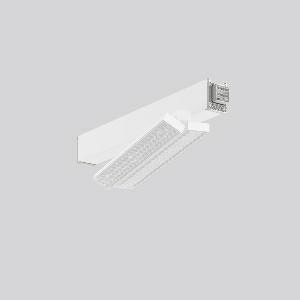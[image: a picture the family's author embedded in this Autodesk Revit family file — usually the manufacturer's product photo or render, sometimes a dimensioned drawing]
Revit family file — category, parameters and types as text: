
# Revit family: linedo_strahlermodule_-_tx-move_950690_842_776_400_4c77
name_source: partatom
category: Lighting Fixtures
units: mm (PartAtom-declared; Revit-internal decimal feet)

## family parameters
Cut with Voids When Loaded = No
Host = Face
Light Source = No
Part Type = Normal
Room Calculation Point = No
Round Connector Dimension = Use Diameter
Shared = No

## types (1)
- MultiLumen 1 (1 x LED Modul 840, 3150 lm, 4000)
    Apparent Load = 41 VA
    CIE Flux Codes = 78 97 99 100 100
    Color Rendering = 80
    Color Temperature = 4000
    Default Elevation = 1800 mm
    Description = LINEDO, 41. 73 W, 6300. 10400 lm, 840, white, DALI
Continuous line luminaire, L 598 B 119 H 131
    Height = 131 mm
    Lamp = 1 x LED Modul 840
    Lamp Light Flux = 3150 lm
    Lamp count = 1
    Length = 598 mm
    Lifetime = 50000 h
    Luminous efficacy = 154 lm/W
    Manufacturer = RZB
    ModVariant = No
    Model = 950690.842.776.400
    Mounting Place = Ceiling
    Mounting Type = Surface mounted
    Number of Poles = 1
    OnlyDefault = Yes
    Power Factor = 1
    Product Name = LINEDO Strahlermodule - TX-MOVE
    Product group = Continuous line luminaire system Linedo IP 54
    ProductGroupID = 314
    Protection Class = Protection class I
    Protection Degree = Degree of protection
    RLX_Detail_Level = 1
    RLX_Emergency_Light_Flux = 0 lm
    RLX_Emergency_Type = 0
    RLX_Emergency_Type_DB = No
    RlxData = <blob elided: 26865 chars, md5=4ce1c273>
    Socket = socket
    Standby Power = 0 W
    System Light Flux = 6300 lm
    System Power = 41 W
    Type Comments = MultiLumen 1
    Type Image = 950690.842.476.400.jpg
    URL = http://relux.com
    VarID = multilumen_1
    Voltage = 0 V
    Weight = 0.00 kg
    Width = 119 mm

## geometry (parser evidence)
native form markers: Blend x4, Sweep x16
no freeform markers — native parametric forms only
